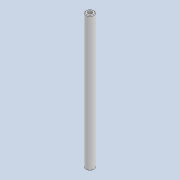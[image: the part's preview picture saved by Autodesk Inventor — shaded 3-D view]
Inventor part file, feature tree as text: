
AUTODESK INVENTOR PART (.ipt)
format: ipt  version: 2020 (Build 240168000, 168)  size: 77,824 bytes
history: native  units: mm
features: extrude x1, chamfer x1, sketch x1
ambient origin geometry x8: Origin, YZ Plane, XZ Plane, XY Plane, X Axis, Y Axis, Z Axis, Center Point
bodies: Solid1 (feature_tree)
feature tree (3):
  extrude  "Extrusion1"  Depth=1.5mm
  chamfer  "Chamfer1"  Distance=50.0mm
  sketch  "Sketch1"  dims[d0=3.0mm d1=1.5mm d2=50.0mm d3=0.0mm d4=0.25mm d5=2.0mm d6=45.0deg]
